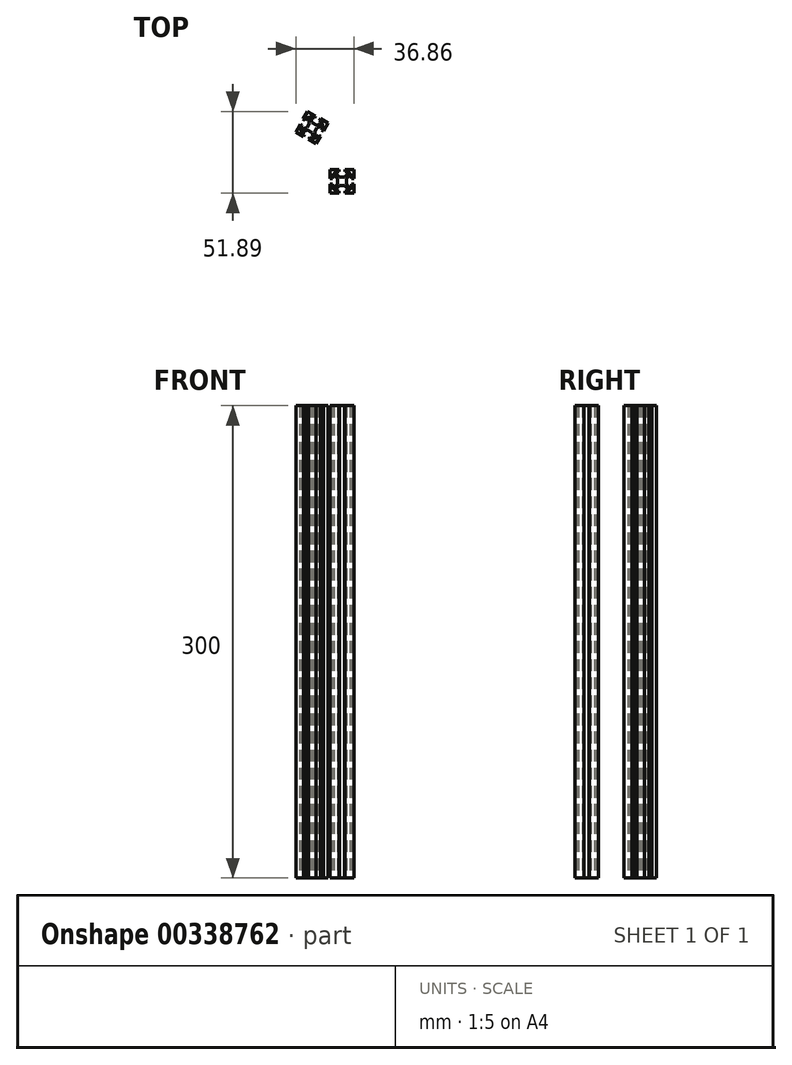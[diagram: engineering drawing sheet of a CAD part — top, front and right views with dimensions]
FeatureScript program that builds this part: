
annotation { "Feature Type Name" : "Feature", "Feature Type Description" : "" }
export const myFeature = defineFeature(function(context is Context, id is Id, definition is map)
    precondition{}
    {
        {
            var Q0;
            Q0=qCreatedBy(makeId("Top.planeOp"),FACE);
            var sketch = newSketch(context, id + "F0", { "sketchPlane" : qUnion([Q0])});
            skLineSegment(sketch, "E0", {"start": v(7.5, -7.5) * mm, "end": v(7.5, -4.3) * mm});
            skLineSegment(sketch, "E1", {"start": v(7.5, -4.3) * mm, "end": v(7.5, -1.79) * mm});
            skLineSegment(sketch, "E2", {"start": v(1.78, -7.5) * mm, "end": v(4.98, -7.5) * mm});
            skLineSegment(sketch, "E3", {"start": v(4.98, -7.5) * mm, "end": v(7.5, -7.5) * mm});
            skLineSegment(sketch, "E4", {"start": v(1.78, -6.1) * mm, "end": v(1.78, -6.88) * mm});
            skLineSegment(sketch, "E5", {"start": v(1.78, -6.88) * mm, "end": v(1.78, -7.5) * mm});
            skLineSegment(sketch, "E6", {"start": v(5.04, -6.1) * mm, "end": v(3.22, -6.1) * mm});
            skLineSegment(sketch, "E7", {"start": v(3.22, -6.1) * mm, "end": v(1.78, -6.1) * mm});
            skLineSegment(sketch, "E8", {"start": v(1.65, -2.7) * mm, "end": v(3.55, -4.6) * mm});
            skLineSegment(sketch, "E9", {"start": v(3.55, -4.6) * mm, "end": v(5.04, -6.1) * mm});
            skLineSegment(sketch, "E10", {"start": v(-1.66, -2.7) * mm, "end": v(0.2, -2.7) * mm});
            skLineSegment(sketch, "E11", {"start": v(0.2, -2.7) * mm, "end": v(1.65, -2.7) * mm});
            skLineSegment(sketch, "E12", {"start": v(-5.04, -6.1) * mm, "end": v(-3.15, -4.2) * mm});
            skLineSegment(sketch, "E13", {"start": v(-3.15, -4.2) * mm, "end": v(-1.66, -2.7) * mm});
            skLineSegment(sketch, "E14", {"start": v(-1.79, -6.1) * mm, "end": v(-3.61, -6.1) * mm});
            skLineSegment(sketch, "E15", {"start": v(-3.61, -6.1) * mm, "end": v(-5.04, -6.1) * mm});
            skLineSegment(sketch, "E16", {"start": v(-1.79, -7.5) * mm, "end": v(-1.79, -6.71) * mm});
            skLineSegment(sketch, "E17", {"start": v(-1.79, -6.71) * mm, "end": v(-1.79, -6.1) * mm});
            skLineSegment(sketch, "E18", {"start": v(-7.5, -7.5) * mm, "end": v(-4.3, -7.5) * mm});
            skLineSegment(sketch, "E19", {"start": v(-4.3, -7.5) * mm, "end": v(-1.79, -7.5) * mm});
            skLineSegment(sketch, "E20", {"start": v(-7.5, -1.79) * mm, "end": v(-7.5, -4.99) * mm});
            skLineSegment(sketch, "E21", {"start": v(-7.5, -4.99) * mm, "end": v(-7.5, -7.5) * mm});
            skLineSegment(sketch, "E22", {"start": v(-6.08, -1.79) * mm, "end": v(-6.88, -1.79) * mm});
            skLineSegment(sketch, "E23", {"start": v(-6.88, -1.79) * mm, "end": v(-7.5, -1.79) * mm});
            skLineSegment(sketch, "E24", {"start": v(-6.08, -5.05) * mm, "end": v(-6.08, -3.22) * mm});
            skLineSegment(sketch, "E25", {"start": v(-6.08, -3.22) * mm, "end": v(-6.08, -1.79) * mm});
            skLineSegment(sketch, "E26", {"start": v(-2.7, -1.68) * mm, "end": v(-4.6, -3.57) * mm});
            skLineSegment(sketch, "E27", {"start": v(-4.6, -3.57) * mm, "end": v(-6.08, -5.05) * mm});
            skLineSegment(sketch, "E28", {"start": v(-2.7, 1.68) * mm, "end": v(-2.7, -0.2) * mm});
            skLineSegment(sketch, "E29", {"start": v(-2.7, -0.2) * mm, "end": v(-2.7, -1.68) * mm});
            skLineSegment(sketch, "E30", {"start": v(-6.08, 5.05) * mm, "end": v(-4.2, 3.16) * mm});
            skLineSegment(sketch, "E31", {"start": v(-4.2, 3.16) * mm, "end": v(-2.7, 1.68) * mm});
            skLineSegment(sketch, "E32", {"start": v(-6.08, 1.79) * mm, "end": v(-6.08, 3.62) * mm});
            skLineSegment(sketch, "E33", {"start": v(-6.08, 3.62) * mm, "end": v(-6.08, 5.05) * mm});
            skLineSegment(sketch, "E34", {"start": v(-7.5, 1.79) * mm, "end": v(-6.7, 1.79) * mm});
            skLineSegment(sketch, "E35", {"start": v(-6.7, 1.79) * mm, "end": v(-6.08, 1.79) * mm});
            skLineSegment(sketch, "E36", {"start": v(-7.5, 7.5) * mm, "end": v(-7.5, 4.3) * mm});
            skLineSegment(sketch, "E37", {"start": v(-7.5, 4.3) * mm, "end": v(-7.5, 1.79) * mm});
            skLineSegment(sketch, "E38", {"start": v(-1.78, 7.5) * mm, "end": v(-4.98, 7.5) * mm});
            skLineSegment(sketch, "E39", {"start": v(-4.98, 7.5) * mm, "end": v(-7.5, 7.5) * mm});
            skLineSegment(sketch, "E40", {"start": v(-1.78, 6.1) * mm, "end": v(-1.78, 6.88) * mm});
            skLineSegment(sketch, "E41", {"start": v(-1.78, 6.88) * mm, "end": v(-1.78, 7.5) * mm});
            skLineSegment(sketch, "E42", {"start": v(-5.04, 6.1) * mm, "end": v(-3.22, 6.1) * mm});
            skLineSegment(sketch, "E43", {"start": v(-3.22, 6.1) * mm, "end": v(-1.78, 6.1) * mm});
            skLineSegment(sketch, "E44", {"start": v(-1.65, 2.7) * mm, "end": v(-3.55, 4.6) * mm});
            skLineSegment(sketch, "E45", {"start": v(-3.55, 4.6) * mm, "end": v(-5.04, 6.1) * mm});
            skLineSegment(sketch, "E46", {"start": v(1.66, 2.7) * mm, "end": v(-0.2, 2.7) * mm});
            skLineSegment(sketch, "E47", {"start": v(-0.2, 2.7) * mm, "end": v(-1.65, 2.7) * mm});
            skLineSegment(sketch, "E48", {"start": v(5.04, 6.1) * mm, "end": v(3.15, 4.2) * mm});
            skLineSegment(sketch, "E49", {"start": v(3.15, 4.2) * mm, "end": v(1.66, 2.7) * mm});
            skLineSegment(sketch, "E50", {"start": v(1.79, 6.1) * mm, "end": v(3.61, 6.1) * mm});
            skLineSegment(sketch, "E51", {"start": v(3.61, 6.1) * mm, "end": v(5.04, 6.1) * mm});
            skLineSegment(sketch, "E52", {"start": v(1.79, 7.5) * mm, "end": v(1.79, 6.71) * mm});
            skLineSegment(sketch, "E53", {"start": v(1.79, 6.71) * mm, "end": v(1.79, 6.1) * mm});
            skLineSegment(sketch, "E54", {"start": v(7.5, 7.5) * mm, "end": v(4.3, 7.5) * mm});
            skLineSegment(sketch, "E55", {"start": v(4.3, 7.5) * mm, "end": v(1.79, 7.5) * mm});
            skLineSegment(sketch, "E56", {"start": v(7.5, 1.79) * mm, "end": v(7.5, 4.99) * mm});
            skLineSegment(sketch, "E57", {"start": v(7.5, 4.99) * mm, "end": v(7.5, 7.5) * mm});
            skLineSegment(sketch, "E58", {"start": v(6.08, 1.79) * mm, "end": v(6.88, 1.79) * mm});
            skLineSegment(sketch, "E59", {"start": v(6.88, 1.79) * mm, "end": v(7.5, 1.79) * mm});
            skLineSegment(sketch, "E60", {"start": v(6.08, 5.05) * mm, "end": v(6.08, 3.22) * mm});
            skLineSegment(sketch, "E61", {"start": v(6.08, 3.22) * mm, "end": v(6.08, 1.79) * mm});
            skLineSegment(sketch, "E62", {"start": v(2.7, 1.68) * mm, "end": v(4.6, 3.57) * mm});
            skLineSegment(sketch, "E63", {"start": v(4.6, 3.57) * mm, "end": v(6.08, 5.05) * mm});
            skLineSegment(sketch, "E64", {"start": v(2.7, -1.68) * mm, "end": v(2.7, 0.2) * mm});
            skLineSegment(sketch, "E65", {"start": v(2.7, 0.2) * mm, "end": v(2.7, 1.68) * mm});
            skLineSegment(sketch, "E66", {"start": v(6.08, -5.05) * mm, "end": v(4.2, -3.16) * mm});
            skLineSegment(sketch, "E67", {"start": v(4.2, -3.16) * mm, "end": v(2.7, -1.68) * mm});
            skLineSegment(sketch, "E68", {"start": v(6.08, -1.79) * mm, "end": v(6.08, -3.62) * mm});
            skLineSegment(sketch, "E69", {"start": v(6.08, -3.62) * mm, "end": v(6.08, -5.05) * mm});
            skLineSegment(sketch, "E70", {"start": v(7.5, -1.79) * mm, "end": v(6.7, -1.79) * mm});
            skLineSegment(sketch, "E71", {"start": v(6.7, -1.79) * mm, "end": v(6.08, -1.79) * mm});
            skSolve(sketch);
        }
        {
            var Q0;
            Q0=makeQuery(id+"F0.imprint","IMPRINT",FACE,{"disambiguationData":[TD([[makeQuery(id+"F0.imprint","IMPRINT",EDGE,{"derivedFrom":sQuery(id+"F0.wireOp",EDGE,"E0")}),1.0]])]});
            extrude(context, id + "F1", {"entities" : qUnion([Q0]), "depth" : 300 * mm});
        }
        {
            var Q0;
            Q0=qCreatedBy(makeId("Top.planeOp"),FACE);
            var sketch = newSketch(context, id + "F2", { "sketchPlane" : qUnion([Q0])});
            skLineSegment(sketch, "E72", {"start": v(-29.36, 31.4) * mm, "end": v(-26.59, 29.8) * mm});
            skLineSegment(sketch, "E73", {"start": v(-26.59, 29.8) * mm, "end": v(-24.4, 28.54) * mm});
            skLineSegment(sketch, "E74", {"start": v(-26.5, 36.35) * mm, "end": v(-28.1, 33.58) * mm});
            skLineSegment(sketch, "E75", {"start": v(-28.1, 33.58) * mm, "end": v(-29.36, 31.4) * mm});
            skLineSegment(sketch, "E76", {"start": v(-25.28, 35.65) * mm, "end": v(-25.96, 36.04) * mm});
            skLineSegment(sketch, "E77", {"start": v(-25.96, 36.04) * mm, "end": v(-26.5, 36.35) * mm});
            skLineSegment(sketch, "E78", {"start": v(-26.9, 32.83) * mm, "end": v(-26, 34.4) * mm});
            skLineSegment(sketch, "E79", {"start": v(-26, 34.4) * mm, "end": v(-25.28, 35.65) * mm});
            skLineSegment(sketch, "E80", {"start": v(-22.28, 34.07) * mm, "end": v(-24.87, 33.37) * mm});
            skLineSegment(sketch, "E81", {"start": v(-24.87, 33.37) * mm, "end": v(-26.9, 32.83) * mm});
            skLineSegment(sketch, "E82", {"start": v(-20.63, 36.93) * mm, "end": v(-21.55, 35.33) * mm});
            skLineSegment(sketch, "E83", {"start": v(-21.55, 35.33) * mm, "end": v(-22.28, 34.07) * mm});
            skLineSegment(sketch, "E84", {"start": v(-21.87, 41.56) * mm, "end": v(-21.17, 38.97) * mm});
            skLineSegment(sketch, "E85", {"start": v(-21.17, 38.97) * mm, "end": v(-20.63, 36.93) * mm});
            skLineSegment(sketch, "E86", {"start": v(-23.5, 38.74) * mm, "end": v(-22.58, 40.32) * mm});
            skLineSegment(sketch, "E87", {"start": v(-22.58, 40.32) * mm, "end": v(-21.87, 41.56) * mm});
            skLineSegment(sketch, "E88", {"start": v(-24.71, 39.44) * mm, "end": v(-24.03, 39.05) * mm});
            skLineSegment(sketch, "E89", {"start": v(-24.03, 39.05) * mm, "end": v(-23.5, 38.74) * mm});
            skLineSegment(sketch, "E90", {"start": v(-21.86, 44.4) * mm, "end": v(-23.45, 41.62) * mm});
            skLineSegment(sketch, "E91", {"start": v(-23.45, 41.62) * mm, "end": v(-24.71, 39.44) * mm});
            skLineSegment(sketch, "E92", {"start": v(-16.9, 41.53) * mm, "end": v(-19.68, 43.13) * mm});
            skLineSegment(sketch, "E93", {"start": v(-19.68, 43.13) * mm, "end": v(-21.86, 44.4) * mm});
            skLineSegment(sketch, "E94", {"start": v(-17.62, 40.3) * mm, "end": v(-17.22, 41) * mm});
            skLineSegment(sketch, "E95", {"start": v(-17.22, 41) * mm, "end": v(-16.9, 41.53) * mm});
            skLineSegment(sketch, "E96", {"start": v(-20.45, 41.94) * mm, "end": v(-18.86, 41.03) * mm});
            skLineSegment(sketch, "E97", {"start": v(-18.86, 41.03) * mm, "end": v(-17.62, 40.3) * mm});
            skLineSegment(sketch, "E98", {"start": v(-19.2, 37.33) * mm, "end": v(-19.9, 39.91) * mm});
            skLineSegment(sketch, "E99", {"start": v(-19.9, 39.91) * mm, "end": v(-20.45, 41.94) * mm});
            skLineSegment(sketch, "E100", {"start": v(-16.3, 35.65) * mm, "end": v(-17.93, 36.6) * mm});
            skLineSegment(sketch, "E101", {"start": v(-17.93, 36.6) * mm, "end": v(-19.2, 37.33) * mm});
            skLineSegment(sketch, "E102", {"start": v(-11.7, 36.89) * mm, "end": v(-14.27, 36.2) * mm});
            skLineSegment(sketch, "E103", {"start": v(-14.27, 36.2) * mm, "end": v(-16.3, 35.65) * mm});
            skLineSegment(sketch, "E104", {"start": v(-14.52, 38.52) * mm, "end": v(-12.94, 37.6) * mm});
            skLineSegment(sketch, "E105", {"start": v(-12.94, 37.6) * mm, "end": v(-11.7, 36.89) * mm});
            skLineSegment(sketch, "E106", {"start": v(-13.81, 39.75) * mm, "end": v(-14.2, 39.06) * mm});
            skLineSegment(sketch, "E107", {"start": v(-14.2, 39.06) * mm, "end": v(-14.52, 38.52) * mm});
            skLineSegment(sketch, "E108", {"start": v(-8.86, 36.9) * mm, "end": v(-11.64, 38.49) * mm});
            skLineSegment(sketch, "E109", {"start": v(-11.64, 38.49) * mm, "end": v(-13.81, 39.75) * mm});
            skLineSegment(sketch, "E110", {"start": v(-11.72, 31.94) * mm, "end": v(-10.12, 34.71) * mm});
            skLineSegment(sketch, "E111", {"start": v(-10.12, 34.71) * mm, "end": v(-8.86, 36.9) * mm});
            skLineSegment(sketch, "E112", {"start": v(-12.94, 32.64) * mm, "end": v(-12.26, 32.25) * mm});
            skLineSegment(sketch, "E113", {"start": v(-12.26, 32.25) * mm, "end": v(-11.72, 31.94) * mm});
            skLineSegment(sketch, "E114", {"start": v(-11.31, 35.46) * mm, "end": v(-12.22, 33.88) * mm});
            skLineSegment(sketch, "E115", {"start": v(-12.22, 33.88) * mm, "end": v(-12.94, 32.64) * mm});
            skLineSegment(sketch, "E116", {"start": v(-15.94, 34.22) * mm, "end": v(-13.35, 34.92) * mm});
            skLineSegment(sketch, "E117", {"start": v(-13.35, 34.92) * mm, "end": v(-11.31, 35.46) * mm});
            skLineSegment(sketch, "E118", {"start": v(-17.6, 31.36) * mm, "end": v(-16.67, 32.96) * mm});
            skLineSegment(sketch, "E119", {"start": v(-16.67, 32.96) * mm, "end": v(-15.94, 34.22) * mm});
            skLineSegment(sketch, "E120", {"start": v(-16.35, 26.73) * mm, "end": v(-17.05, 29.32) * mm});
            skLineSegment(sketch, "E121", {"start": v(-17.05, 29.32) * mm, "end": v(-17.6, 31.36) * mm});
            skLineSegment(sketch, "E122", {"start": v(-14.72, 29.55) * mm, "end": v(-15.64, 27.97) * mm});
            skLineSegment(sketch, "E123", {"start": v(-15.64, 27.97) * mm, "end": v(-16.35, 26.73) * mm});
            skLineSegment(sketch, "E124", {"start": v(-13.5, 28.85) * mm, "end": v(-14.19, 29.24) * mm});
            skLineSegment(sketch, "E125", {"start": v(-14.19, 29.24) * mm, "end": v(-14.72, 29.55) * mm});
            skLineSegment(sketch, "E126", {"start": v(-16.36, 23.9) * mm, "end": v(-14.77, 26.67) * mm});
            skLineSegment(sketch, "E127", {"start": v(-14.77, 26.67) * mm, "end": v(-13.5, 28.85) * mm});
            skLineSegment(sketch, "E128", {"start": v(-21.31, 26.76) * mm, "end": v(-18.54, 25.16) * mm});
            skLineSegment(sketch, "E129", {"start": v(-18.54, 25.16) * mm, "end": v(-16.36, 23.9) * mm});
            skLineSegment(sketch, "E130", {"start": v(-20.6, 27.98) * mm, "end": v(-21, 27.3) * mm});
            skLineSegment(sketch, "E131", {"start": v(-21, 27.3) * mm, "end": v(-21.31, 26.76) * mm});
            skLineSegment(sketch, "E132", {"start": v(-17.77, 26.35) * mm, "end": v(-19.36, 27.27) * mm});
            skLineSegment(sketch, "E133", {"start": v(-19.36, 27.27) * mm, "end": v(-20.6, 27.98) * mm});
            skLineSegment(sketch, "E134", {"start": v(-19.01, 30.96) * mm, "end": v(-18.32, 28.38) * mm});
            skLineSegment(sketch, "E135", {"start": v(-18.32, 28.38) * mm, "end": v(-17.77, 26.35) * mm});
            skLineSegment(sketch, "E136", {"start": v(-21.92, 32.64) * mm, "end": v(-20.29, 31.7) * mm});
            skLineSegment(sketch, "E137", {"start": v(-20.29, 31.7) * mm, "end": v(-19.01, 30.96) * mm});
            skLineSegment(sketch, "E138", {"start": v(-26.53, 31.4) * mm, "end": v(-23.95, 32.1) * mm});
            skLineSegment(sketch, "E139", {"start": v(-23.95, 32.1) * mm, "end": v(-21.92, 32.64) * mm});
            skLineSegment(sketch, "E140", {"start": v(-23.7, 29.77) * mm, "end": v(-25.28, 30.69) * mm});
            skLineSegment(sketch, "E141", {"start": v(-25.28, 30.69) * mm, "end": v(-26.53, 31.4) * mm});
            skLineSegment(sketch, "E142", {"start": v(-24.4, 28.54) * mm, "end": v(-24.01, 29.23) * mm});
            skLineSegment(sketch, "E143", {"start": v(-24.01, 29.23) * mm, "end": v(-23.7, 29.77) * mm});
            skSolve(sketch);
        }
        {
            var Q0;
            Q0=makeQuery(id+"F2.imprint","IMPRINT",FACE,{"disambiguationData":[TD([[makeQuery(id+"F2.imprint","IMPRINT",EDGE,{"derivedFrom":sQuery(id+"F2.wireOp",EDGE,"E72")}),1.0]])]});
            extrude(context, id + "F3", {"entities" : qUnion([Q0]), "depth" : 300 * mm});
        }
    });
